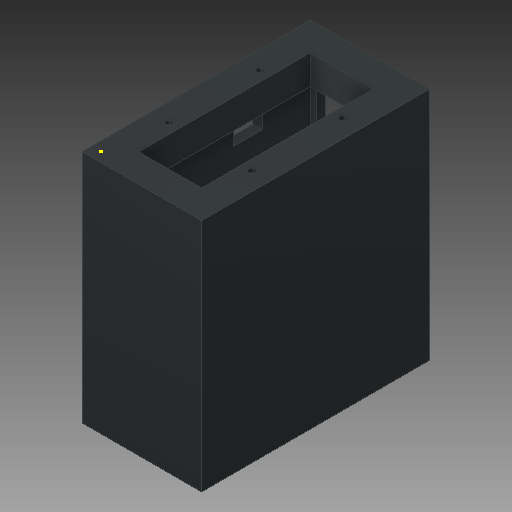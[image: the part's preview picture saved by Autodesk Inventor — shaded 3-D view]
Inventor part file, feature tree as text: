
AUTODESK INVENTOR PART (.ipt)
format: ipt  version: 2018 (Build 220112000, 112)  size: 162,816 bytes
history: native  units: mm
features: sketch x6, extrude x5
ambient origin geometry x8: Origin, YZ Plane, XZ Plane, XY Plane, X Axis, Y Axis, Z Axis, Center Point
bodies: Solid1 (feature_tree)
feature tree (11):
  extrude  "Extrusion1"  Depth=520.0mm
  extrude  "Extrusion2"  Depth=583.0mm TaperAngle=0.0deg
  extrude  "Extrusion3"  Depth=440.0mm
  sketch  "Sketch4"  dims[d7=77.0mm d8=38.0mm]
  extrude  "Extrusion4"  Depth=38.0mm
  extrude  "Extrusion5"  Depth=70.0mm
  sketch  "Sketch1"  dims[d0=250.0mm d1=520.0mm]
  sketch  "Sketch2"  dims[d2=23.0mm d3=583.0mm d4=0.0mm]
  sketch  "Sketch3"  dims[d5=220.0mm d6=440.0mm]
  sketch  "Sketch5"  dims[d9=583.0mm d10=0.0mm d11=70.0mm]
  sketch  "Sketch6"  dims[d12=80.0mm d13=430.0mm d14=143.0mm d15=583.0mm d16=0.0mm d17=47.0mm d18=583.0mm d19=0.0mm d20=16.0mm d21=170.0mm d22=45.0mm d23=16.0mm d24=170.0mm d25=45.0mm d26=10.0mm d27=0.0mm]
